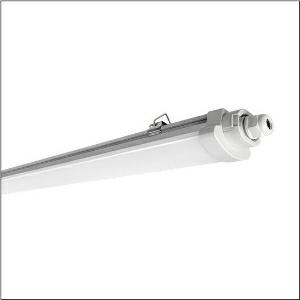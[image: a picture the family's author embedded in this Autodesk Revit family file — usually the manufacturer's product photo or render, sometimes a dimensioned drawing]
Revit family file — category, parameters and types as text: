
# Revit family: monsun_r__41_51fk20mk440a_a1bd
name_source: partatom
category: Lighting Fixtures
units: mm (PartAtom-declared; Revit-internal decimal feet)

## family parameters
Cut with Voids When Loaded = No
Host = Face
Light Source = No
Part Type = Normal
Room Calculation Point = No
Round Connector Dimension = Use Diameter
Shared = No

## types (1)
- --- (1 x LED, 4000 lm, 30 W, 4000K)
    Apparent Load = 30 VA
    CIE Flux Codes = 44 74 92 92 100
    Color Rendering = 80
    Color Temperature = 4000K
    Default Elevation = 1800 mm
    Description = Monsun® 41, damp-proof luminaire, primary optical cover: diffuser, of PC, frosted, light emission: direct distribution, primary light characteristic: symmetric, installation type: surface-mounted, suspended mounting, LED, rated luminous flux: 4.000lm, luminous efficacy: 130lm/W, light colour: 840, colour temperature: 4000K, control gear: ON/OFF Multilumen, with terminal, 3-pole, mains connection: 220..240V, AC, 50/60Hz, rated input power: 30W, housing, luminaire housing, of PC, grey, length: 1.200mm, width: 79mm, height: 52mm, end cap, of PC, grey, ceiling mounting element, of stainless steel (V2A), protection rating (complete): IP65, insulation class (complete): insulation class II (safety insulation), certification: CE, UKCA, protection symbol: D, impact resistance: IK08, permissible operating ambient temperature: -20..+35°C, corresponds to IFS (International Featured Standards) requirements for safety and quality in the food industry, contact your sales advisor before using the luminaires in applications with unclear chemical exposure, large temperature fluctuations or condensation-forming humidity, packaging unit: 1 piece
    Height = 54 mm
    Lamp = 1 x LED
    Lamp Light Flux = 4000 lm
    Lamp Power = 30 W
    Lamp count = 1
    Length = 1200 mm
    Luminous efficacy = 133 lm/W
    Manufacturer = Siteco
    ModVariant = No
    Model = 51FK20MK440A
    Mounting Place = Ceiling
    Mounting Type = Surface mounted
    Number of Poles = 1
    OnlyDefault = Yes
    Power Factor = 1
    Product Name = Monsun® 41
    Product group = damp-proof luminaire
    ProductGroupID = 301
    Protection Class = Protection class II
    Protection Degree = IP 65
    RLX_Detail_Level = 1
    RLX_Emergency_Light_Flux = 0 lm
    RLX_Emergency_Type = 0
    RLX_Emergency_Type_DB = No
    RlxData = <blob elided: 31813 chars, md5=a72cce9d>
    Socket = socket
    Standby Power = 0 W
    System Light Flux = 4000 lm
    System Power = 30 W
    Type Comments = factory setting: luminous flux: 100 % | (HIGH)
    Type Image = l_1007037.jpg
    URL = http://relux.com
    VarID = @adj_196175
    Voltage = 0 V
    Weight = 0.00 kg
    Width = 79 mm

## geometry (parser evidence)
native form markers: Blend x4, Sweep x13
no freeform markers — native parametric forms only
